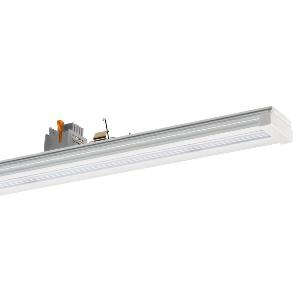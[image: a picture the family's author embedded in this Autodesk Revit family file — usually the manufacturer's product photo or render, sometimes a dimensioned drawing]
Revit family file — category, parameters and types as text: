
# Revit family: conveo_-_cvg_4500_840_xn-p_da_7_226848139-00804951_c8b8
name_source: partatom
category: Lighting Fixtures
units: mm (PartAtom-declared; Revit-internal decimal feet)

## family parameters
Cut with Voids When Loaded = No
Host = Face
Light Source = No
Part Type = Normal
Room Calculation Point = No
Round Connector Dimension = Use Diameter
Shared = No

## types (1)
- CONVEO - CVG 4500/840/xN-P/DA/7 (1 x LED, 4200 lm, 4000K)
    Apparent Load = 28 VA
    Approval mark = CE
    CIE Flux Codes = 57 84 97 100 100
    Color Rendering = 80-89
    Color Temperature = 4000K
    Control Gear = Electronic ballast
    Default Elevation = 1800 mm
    Description = CVG 4500/840/xN-P/DA/7|Continuous-row system|light source: LED|work equipment: Adjustable electronic ballast, digital DALI|connected load: 220-240 V, 50-60 Hz|Power consumption: approx. 28 W|luminous flux: 4200 lm|luminous efficacy: 150 lm/W|colour temperature: Cold white, ca. 4000 K|color rendering index (CRI): >= 80|chromaticity tolerance:  3 SDCM|System of protection: IP 54|class of protection: I|technology: Continuously dimmable|luminaire body|material: Aluminium|surface: Powder coatet|colour: White|lamp cover: Acrylic (PMMA), Satine|weight (net): approx. 1.9 kg|Fastening: Available separately|minimum ambient temperature: -25 ░C|maximum ambient temperature: 55 ░C|glare control: Prism optics (linear)|Approval mark: VDE - ENEC|
    Frequency = 50 Hz
    Height = 70 mm
    Lamp = 1 x LED
    Lamp Light Flux = 4200 lm
    Lamp count = 1
    Length = 1500 mm
    Luminous efficacy = 150 lm/W
    Manufacturer = Waldmann
    ModVariant = No
    Model = 226848139-00804951
    Mounting Place = Ceiling
    Mounting Type = Pendant
    Number of Poles = 1
    OnlyDefault = Yes
    Power Factor = 1
    Product Name = CONVEO - CVG 4500/840/xN-P/DA/7
    Product group = Continuous-row system (industry)
    ProductGroupID = 301
    Protection Class = Protection class I
    Protection Degree = IP 54
    RLX_Detail_Level = 1
    RlxData = <blob elided: 99833 chars, md5=646ea690>
    Socket = socket
    Standby Power = 0 W
    System Light Flux = 4200 lm
    System Power = 28 W
    Type Comments = Product without accessories
    Type Image = 226848019-00804937-1p7.jpg
    URL = http://relux.com
    VarID = ---
    Voltage = 230 V
    Voltage Range = 220-240 V
    Weight = 0.00 kg
    Width = 64 mm

## geometry (parser evidence)
native form markers: Blend x4, Sweep x11
no freeform markers — native parametric forms only
